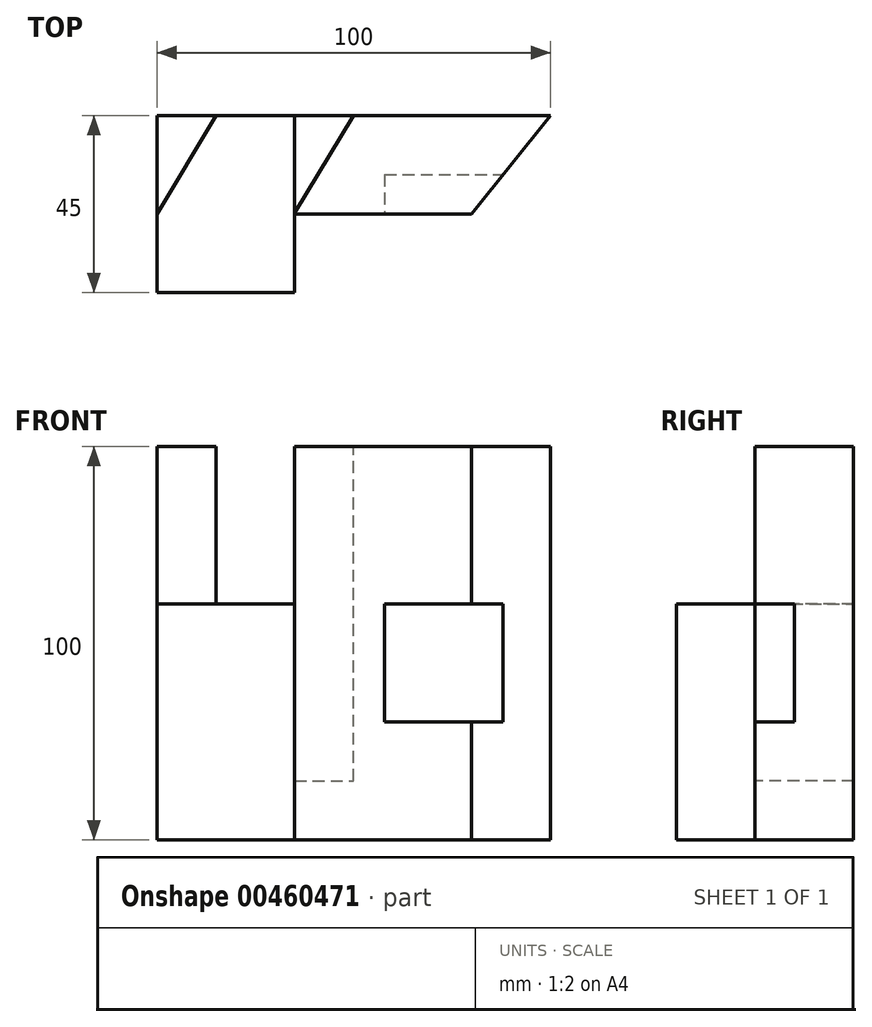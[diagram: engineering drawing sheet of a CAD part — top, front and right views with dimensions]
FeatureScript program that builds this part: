
annotation { "Feature Type Name" : "Feature", "Feature Type Description" : "" }
export const myFeature = defineFeature(function(context is Context, id is Id, definition is map)
    precondition{}
    {
        {
            var Q0;
            Q0=qCreatedBy(makeId("Front.planeOp"),FACE);
            var sketch = newSketch(context, id + "F0", { "sketchPlane" : qUnion([Q0])});
            skLineSegment(sketch, "E0.bottom", {"start": v(0, 0) * mm, "end": v(-100, 0) * mm});
            skLineSegment(sketch, "E0.top", {"start": v(0, 100) * mm, "end": v(-100, 100) * mm});
            skLineSegment(sketch, "E0.left", {"start": v(0, 0) * mm, "end": v(0, 100) * mm});
            skLineSegment(sketch, "E0.right", {"start": v(-100, 0) * mm, "end": v(-100, 100) * mm});
            skSolve(sketch);
        }
        {
            var Q0;
            Q0=makeQuery(id+"F0.imprint","IMPRINT",FACE,{"disambiguationData":[TD([[makeQuery(id+"F0.imprint","IMPRINT",EDGE,{"derivedFrom":sQuery(id+"F0.wireOp",EDGE,"E0.bottom")}),-1.0]])]});
            extrude(context, id + "F1", {"entities" : qUnion([Q0]), "depth" : 45 * mm});
        }
        {
            var Q0;
            Q0=makeQuery(id+"F1.opExtrude","SWEPT_FACE",FACE,{"disambiguationData":[OSD([sQuery(id+"F0.wireOp",EDGE,"E0.top")])]});
            var sketch = newSketch(context, id + "F2", { "sketchPlane" : qUnion([Q0])});
            skLineSegment(sketch, "E1", {"start": v(-100, 0) * mm, "end": v(-85, 0) * mm});
            skLineSegment(sketch, "E2", {"start": v(-85, 0) * mm, "end": v(-100, -25) * mm});
            skLineSegment(sketch, "E3", {"start": v(-100, -25) * mm, "end": v(-100, 0) * mm});
            skLineSegment(sketch, "E4.bottom", {"start": v(0, -45) * mm, "end": v(-65, -45) * mm});
            skLineSegment(sketch, "E4.top", {"start": v(0, -25) * mm, "end": v(-65, -25) * mm});
            skLineSegment(sketch, "E4.left", {"start": v(0, -45) * mm, "end": v(0, -25) * mm});
            skLineSegment(sketch, "E4.right", {"start": v(-65, -45) * mm, "end": v(-65, -25) * mm});
            skLineSegment(sketch, "E5", {"start": v(-65, -25) * mm, "end": v(-65, 0) * mm});
            skSolve(sketch);
        }
        {
            var Q0;
            Q0=makeQuery(id+"F2.imprint","IMPRINT",FACE,{"disambiguationData":[TD([[makeQuery(id+"F2.imprint","IMPRINT",EDGE,{"derivedFrom":sQuery(id+"F2.wireOp",EDGE,"E4.bottom")}),-1.0]])]});
            extrude(context, id + "F3", {"entities" : qUnion([Q0]), "operationType" : NewBodyOperationType.REMOVE, "endBound" : BoundingType.UP_TO_NEXT, "oppositeDirection" : true, "depth" : 25 * mm});
        }
        {
            var Q0;
            Q0=makeQuery(id+"F1.opExtrude","SWEPT_FACE",FACE,{"disambiguationData":[OSD([sQuery(id+"F0.wireOp",EDGE,"E0.top")])]});
            var sketch = newSketch(context, id + "F4", { "sketchPlane" : qUnion([Q0])});
            skLineSegment(sketch, "E6", {"start": v(0, 0) * mm, "end": v(-20, -25) * mm});
            skLineSegment(sketch, "E7", {"start": v(-20, -25) * mm, "end": v(0, -25) * mm});
            skLineSegment(sketch, "E8", {"start": v(0, -25) * mm, "end": v(0, 0) * mm});
            skSolve(sketch);
        }
        {
            var Q0;
            Q0=makeQuery(id+"F4.imprint","IMPRINT",FACE,{"disambiguationData":[TD([[makeQuery(id+"F4.imprint","IMPRINT",EDGE,{"derivedFrom":sQuery(id+"F4.wireOp",EDGE,"E6")}),1.0]])]});
            extrude(context, id + "F5", {"entities" : qUnion([Q0]), "operationType" : NewBodyOperationType.REMOVE, "endBound" : BoundingType.UP_TO_NEXT, "oppositeDirection" : true, "depth" : 25 * mm});
        }
        {
            var Q0;
            Q0=qCreatedBy(makeId("Top.planeOp"),FACE);
            cPlane(context, id + "F6", {"entities" : qUnion([Q0]), "cplaneType" : CPlaneType.OFFSET, "offset" : 60 * mm, "width" : 150 * mm, "height" : 150 * mm});
        }
        {
            var Q0;
            {var subQ4=sQuery(id+"F2.wireOp",EDGE,"E2");Q0=makeQuery(id+"F2.imprint","IMPRINT",FACE,{"disambiguationData":[TD([[makeQuery(id+"F2.imprint","IMPRINT",EDGE,{"derivedFrom":subQ4}),1.0]])]});}
            var Q1;
            Q1=qCreatedBy(id+"F6.planeOp",FACE);
            extrude(context, id + "F7", {"entities" : qUnion([Q0]), "operationType" : NewBodyOperationType.REMOVE, "endBound" : BoundingType.UP_TO_SURFACE, "oppositeDirection" : true, "endBoundEntityFace" : qUnion([Q1]), "depth" : 25 * mm});
        }
        {
            var Q0;
            {var subQ0=sQuery(id+"F0.wireOp",EDGE,"E0.top");Q0=makeQuery(id+"F7.boolean.opBoolean","SPLIT",FACE,{"disambiguationData":[TD([makeQuery(id+"F3.boolean.opBoolean","COPY",FACE,{"derivedFrom":makeQuery(id+"F3.opExtrude","SWEPT_FACE",FACE,{"disambiguationData":[OSD([sQuery(id+"F2.wireOp",EDGE,"E4.top")])]})})])],"derivedFrom":makeQuery(id+"F1.opExtrude","SWEPT_FACE",FACE,{"disambiguationData":[OSD([subQ0])]})});}
            var sketch = newSketch(context, id + "F8", { "sketchPlane" : qUnion([Q0])});
            skLineSegment(sketch, "E9", {"start": v(-65, 0) * mm, "end": v(-50, 0) * mm});
            skLineSegment(sketch, "E10", {"start": v(-50, 0) * mm, "end": v(-65, -24.8) * mm});
            skLineSegment(sketch, "E11", {"start": v(-65, -24.8) * mm, "end": v(-65, 0) * mm});
            skSolve(sketch);
        }
        {
            var Q0;
            Q0=qCreatedBy(makeId("Top.planeOp"),FACE);
            cPlane(context, id + "F9", {"entities" : qUnion([Q0]), "cplaneType" : CPlaneType.OFFSET, "offset" : 15 * mm, "width" : 150 * mm, "height" : 150 * mm});
        }
        {
            var Q0;
            Q0=makeQuery(id+"F8.imprint","IMPRINT",FACE,{"disambiguationData":[TD([[makeQuery(id+"F8.imprint","IMPRINT",EDGE,{"derivedFrom":sQuery(id+"F8.wireOp",EDGE,"E9")}),1.0]])]});
            var Q1;
            Q1=qCreatedBy(id+"F9.planeOp",FACE);
            extrude(context, id + "F10", {"entities" : qUnion([Q0]), "operationType" : NewBodyOperationType.REMOVE, "endBound" : BoundingType.UP_TO_SURFACE, "oppositeDirection" : true, "endBoundEntityFace" : qUnion([Q1]), "depth" : 25 * mm});
        }
        {
            var Q0;
            Q0=makeQuery(id+"F3.boolean.opBoolean","COPY",FACE,{"derivedFrom":makeQuery(id+"F3.opExtrude","SWEPT_FACE",FACE,{"disambiguationData":[OSD([sQuery(id+"F2.wireOp",EDGE,"E4.top")])]})});
            var sketch = newSketch(context, id + "F11", { "sketchPlane" : qUnion([Q0])});
            skLineSegment(sketch, "E12.bottom", {"start": v(-42.14, 60) * mm, "end": v(-5.36, 60) * mm});
            skLineSegment(sketch, "E12.top", {"start": v(-42.14, 30) * mm, "end": v(-5.36, 30) * mm});
            skLineSegment(sketch, "E12.left", {"start": v(-42.14, 60) * mm, "end": v(-42.14, 30) * mm});
            skLineSegment(sketch, "E12.right", {"start": v(-5.36, 60) * mm, "end": v(-5.36, 30) * mm});
            skSolve(sketch);
        }
        {
            var Q0;
            {var subQ0=sQuery(id+"F11.wireOp",EDGE,"E12.right");Q0=makeQuery(id+"F11.imprint","IMPRINT",FACE,{"disambiguationData":[TD([[makeQuery(id+"F11.imprint","IMPRINT",EDGE,{"derivedFrom":subQ0}),-1.0]])]});}
            var Q1;
            {var subQ0=sQuery(id+"F11.wireOp",EDGE,"E12.left");Q1=makeQuery(id+"F11.imprint","IMPRINT",FACE,{"disambiguationData":[TD([[makeQuery(id+"F11.imprint","IMPRINT",EDGE,{"derivedFrom":subQ0}),1.0]])]});}
            extrude(context, id + "F12", {"entities" : qUnion([Q0, Q1]), "operationType" : NewBodyOperationType.REMOVE, "oppositeDirection" : true, "depth" : 10 * mm});
        }
    });
